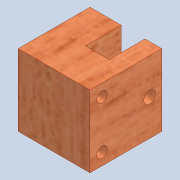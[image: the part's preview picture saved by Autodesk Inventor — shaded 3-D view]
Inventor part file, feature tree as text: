
AUTODESK INVENTOR PART (.ipt)
format: ipt  version: 2020 (Build 240168000, 168)  size: 163,328 bytes
history: native  units: mm
features: sketch x5, extrude x3, hole x2
ambient origin geometry x8: Origin, YZ Plane, XZ Plane, XY Plane, X Axis, Y Axis, Z Axis, Center Point
bodies: Solid1 (feature_tree)
feature tree (10):
  extrude  "Extrusion1"  Depth=30.0mm
  extrude  "Extrusion4"  Depth=10.0mm
  extrude  "Extrusion3"  Depth=15.0mm
  hole  "Hole1"  [1 undecoded]
  hole  "Hole2"  [1 undecoded]
  sketch  "Sketch1"  dims[d0=30.0mm d1=30.0mm]
  sketch  "Sketch4"  dims[d2=30.0mm d3=0.0mm d8=10.0mm]
  sketch  "Sketch5"  dims[d9=15.0mm d10=0.0mm d11=5.0mm]
  sketch  "Sketch6"  dims[d12=5.0mm d13=6.0mm d14=4.0mm d15=2.0mm d16=90.0deg d17=10.0mm d18=20.594885mm d19=4.5mm]
  sketch  "Sketch7"  dims[d20=5.0mm d21=5.0mm d22=5.0mm d23=0.0mm d24=0.0mm d25=7.0mm d26=4.134mm d27=10.0mm d28=4.0mm d29=2.0mm d30=90.0deg d31=10.0mm d32=20.594885mm]
note: 2 required parameter values undecoded (feature->parameter linkage not recoverable at this tier; creation-order binding heuristic only, values carry confidence <= 0.55)
